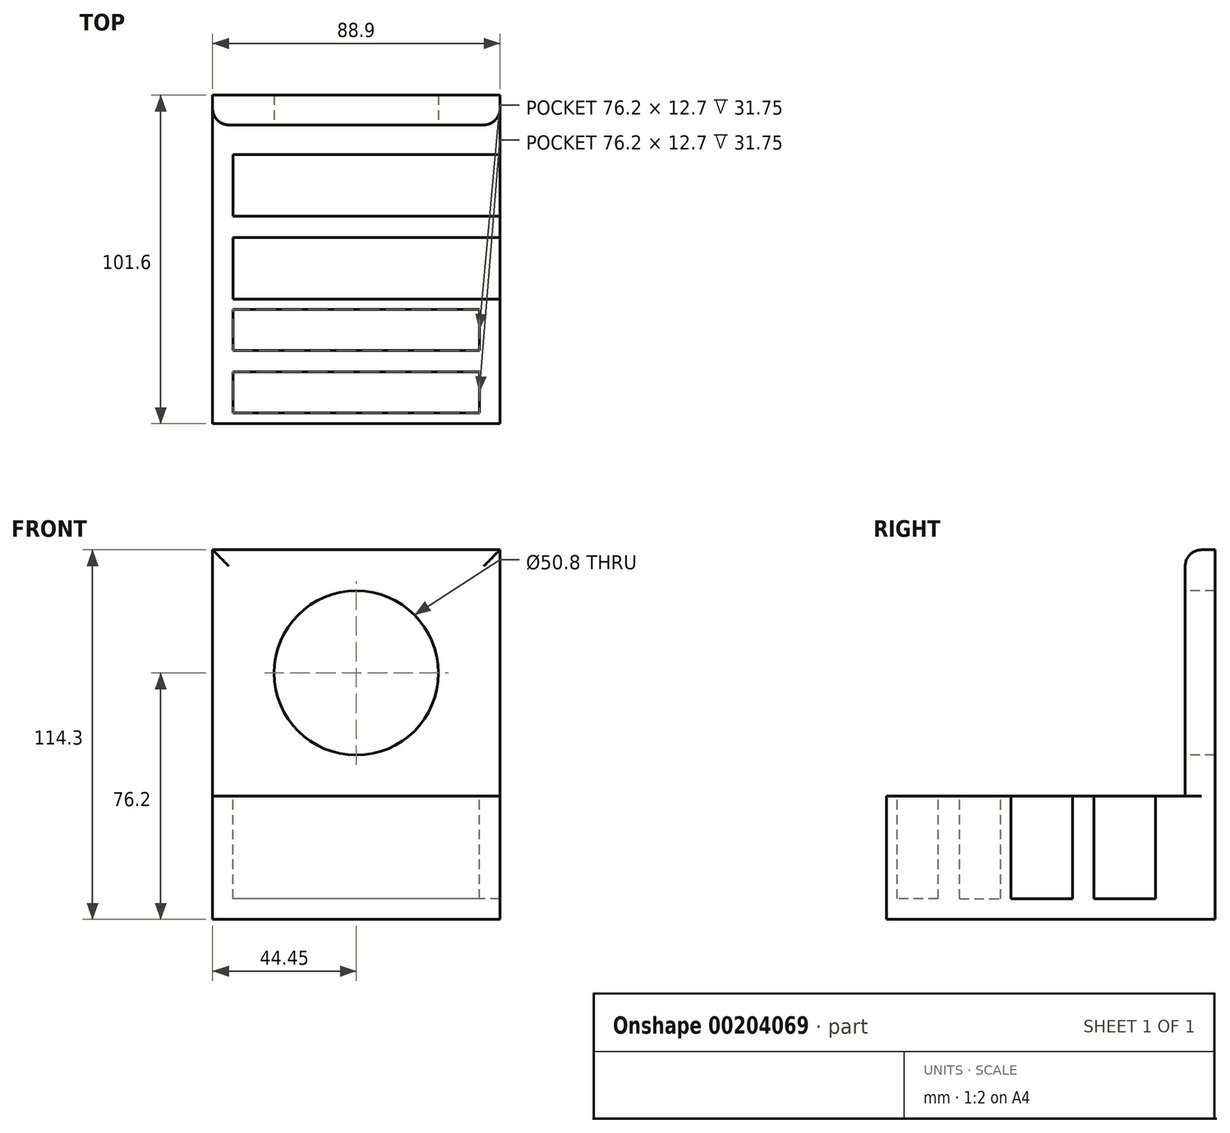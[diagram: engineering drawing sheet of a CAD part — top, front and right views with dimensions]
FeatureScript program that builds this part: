
annotation { "Feature Type Name" : "Feature", "Feature Type Description" : "" }
export const myFeature = defineFeature(function(context is Context, id is Id, definition is map)
    precondition{}
    {
        {
            var Q0;
            Q0=qCreatedBy(makeId("Front.planeOp"),FACE);
            var sketch = newSketch(context, id + "F0", { "sketchPlane" : qUnion([Q0])});
            skLineSegment(sketch, "E0", {"start": v(0, 19.05) * mm, "end": v(-44.45, 19.05) * mm});
            skLineSegment(sketch, "E1", {"start": v(-44.45, 19.05) * mm, "end": v(-44.45, 0) * mm});
            skLineSegment(sketch, "E2.MirrorCS", {"start": v(44.45, 19.05) * mm, "end": v(44.45, 0) * mm});
            skLineSegment(sketch, "E3.MirrorCS", {"start": v(0, 19.05) * mm, "end": v(44.45, 19.05) * mm});
            skLineSegment(sketch, "E4.MirrorCS", {"start": v(-44.45, -19.05) * mm, "end": v(-44.45, 0) * mm});
            skLineSegment(sketch, "E5.MirrorCS", {"start": v(0, -19.05) * mm, "end": v(-44.45, -19.05) * mm});
            skLineSegment(sketch, "E6.MirrorCS", {"start": v(0, -19.05) * mm, "end": v(44.45, -19.05) * mm});
            skLineSegment(sketch, "E7.MirrorCS", {"start": v(44.45, -19.05) * mm, "end": v(44.45, 0) * mm});
            skSolve(sketch);
        }
        {
            var Q0;
            Q0 = qSketchRegion(id + "F0", true);
            extrude(context, id + "F1", {"entities" : qUnion([Q0]), "depth" : 101.6 * mm});
        }
        {
            var Q0;
            Q0=makeQuery(id+"F1.opExtrude","SWEPT_FACE",FACE,{"disambiguationData":[OSD([sQuery(id+"F0.wireOp",EDGE,"E0"),sQuery(id+"F0.wireOp",EDGE,"E3.MirrorCS")])]});
            var sketch = newSketch(context, id + "F2", { "sketchPlane" : qUnion([Q0])});
            skLineSegment(sketch, "E8", {"start": v(0, 0) * mm, "end": v(0, -101.6) * mm, "construction": true});
            skLineSegment(sketch, "E9", {"start": v(0, -85.6) * mm, "end": v(-38.1, -85.6) * mm});
            skLineSegment(sketch, "E10", {"start": v(-38.1, -85.6) * mm, "end": v(-38.1, -98.3) * mm});
            skLineSegment(sketch, "E11", {"start": v(-38.1, -98.3) * mm, "end": v(0, -98.3) * mm});
            skLineSegment(sketch, "E12.MirrorCS", {"start": v(0, -85.6) * mm, "end": v(38.1, -85.6) * mm});
            skLineSegment(sketch, "E13.MirrorCS", {"start": v(38.1, -85.6) * mm, "end": v(38.1, -98.3) * mm});
            skLineSegment(sketch, "E14.MirrorCS", {"start": v(38.1, -98.3) * mm, "end": v(0, -98.3) * mm});
            skLineSegment(sketch, "E15", {"start": v(-44.45, -82.3) * mm, "end": v(44.45, -82.3) * mm, "construction": true});
            skLineSegment(sketch, "E16.MirrorCS", {"start": v(0, -79) * mm, "end": v(-38.1, -79) * mm});
            skLineSegment(sketch, "E17.MirrorCS", {"start": v(0, -79) * mm, "end": v(38.1, -79) * mm});
            skLineSegment(sketch, "E18.MirrorCS", {"start": v(38.1, -79) * mm, "end": v(38.1, -66.3) * mm});
            skLineSegment(sketch, "E19.MirrorCS", {"start": v(38.1, -66.3) * mm, "end": v(0, -66.3) * mm});
            skLineSegment(sketch, "E20.MirrorCS", {"start": v(-38.1, -66.3) * mm, "end": v(0, -66.3) * mm});
            skLineSegment(sketch, "E21.MirrorCS", {"start": v(-38.1, -79) * mm, "end": v(-38.1, -66.3) * mm});
            skSolve(sketch);
        }
        {
            var Q0;
            Q0 = qSketchRegion(id + "F2", true);
            extrude(context, id + "F3", {"entities" : qUnion([Q0]), "operationType" : NewBodyOperationType.REMOVE, "oppositeDirection" : true, "depth" : 31.75 * mm});
        }
        {
            var Q0;
            Q0=makeQuery(id+"F1.opExtrude","SWEPT_FACE",FACE,{"disambiguationData":[OSD([sQuery(id+"F0.wireOp",EDGE,"E1"),sQuery(id+"F0.wireOp",EDGE,"E4.MirrorCS")])]});
            var sketch = newSketch(context, id + "F4", { "sketchPlane" : qUnion([Q0])});
            skLineSegment(sketch, "E22.0.0", {"start": v(79, 19.05) * mm, "end": v(66.3, 19.05) * mm, "construction": true});
            skLineSegment(sketch, "E22.0.1", {"start": v(66.3, 19.05) * mm, "end": v(66.3, -12.7) * mm, "construction": true});
            skLineSegment(sketch, "E22.0.2", {"start": v(66.3, -12.7) * mm, "end": v(79, -12.7) * mm, "construction": true});
            skLineSegment(sketch, "E22.0.3", {"start": v(79, -12.7) * mm, "end": v(79, 19.05) * mm, "construction": true});
            skLineSegment(sketch, "E23.bottom", {"start": v(44.07, 19.05) * mm, "end": v(63.12, 19.05) * mm});
            skLineSegment(sketch, "E23.top", {"start": v(44.07, -12.7) * mm, "end": v(63.12, -12.7) * mm});
            skLineSegment(sketch, "E23.left", {"start": v(44.07, 19.05) * mm, "end": v(44.07, -12.7) * mm});
            skLineSegment(sketch, "E23.right", {"start": v(63.12, 19.05) * mm, "end": v(63.12, -12.7) * mm});
            skLineSegment(sketch, "E24", {"start": v(40.77, 19.05) * mm, "end": v(40.77, -19.05) * mm, "construction": true});
            skLineSegment(sketch, "E25.MirrorCS", {"start": v(37.47, 19.05) * mm, "end": v(18.42, 19.05) * mm});
            skLineSegment(sketch, "E26.MirrorCS", {"start": v(37.47, 19.05) * mm, "end": v(37.47, -12.7) * mm});
            skLineSegment(sketch, "E27.MirrorCS", {"start": v(37.47, -12.7) * mm, "end": v(18.42, -12.7) * mm});
            skLineSegment(sketch, "E28.MirrorCS", {"start": v(18.42, 19.05) * mm, "end": v(18.42, -12.7) * mm});
            skSolve(sketch);
        }
        {
            var Q0;
            Q0 = qSketchRegion(id + "F4", true);
            extrude(context, id + "F5", {"entities" : qUnion([Q0]), "operationType" : NewBodyOperationType.REMOVE, "endBound" : BoundingType.THROUGH_ALL, "oppositeDirection" : true, "depth" : 25.4 * mm});
        }
        {
            var Q0;
            {var subQ2=sQuery(id+"F0.wireOp",EDGE,"E3.MirrorCS");var subQ5=sQuery(id+"F0.wireOp",EDGE,"E0");Q0=makeQuery(id+"F5.boolean.opBoolean","SPLIT",FACE,{"disambiguationData":[TD([makeQuery(id+"F5.opExtrude","SWEPT_FACE",FACE,{"disambiguationData":[OSD([sQuery(id+"F4.wireOp",EDGE,"E28.MirrorCS")])]})])],"derivedFrom":makeQuery(id+"F1.opExtrude","SWEPT_FACE",FACE,{"disambiguationData":[OSD([subQ5,subQ2])]})});}
            var sketch = newSketch(context, id + "F6", { "sketchPlane" : qUnion([Q0])});
            skLineSegment(sketch, "E29.bottom", {"start": v(-44.45, 0) * mm, "end": v(44.45, 0) * mm});
            skLineSegment(sketch, "E29.top", {"start": v(-44.45, -9.2) * mm, "end": v(44.45, -9.2) * mm});
            skLineSegment(sketch, "E29.left", {"start": v(-44.45, 0) * mm, "end": v(-44.45, -9.2) * mm});
            skLineSegment(sketch, "E29.right", {"start": v(44.45, 0) * mm, "end": v(44.45, -9.2) * mm});
            skSolve(sketch);
        }
        {
            var Q0;
            Q0 = qSketchRegion(id + "F6", true);
            extrude(context, id + "F7", {"entities" : qUnion([Q0]), "operationType" : NewBodyOperationType.ADD, "depth" : 76.2 * mm});
        }
        {
            var Q0;
            Q0=makeQuery(id+"F7.boolean.opBoolean","MERGE",FACE,{"derivedFrom":[makeQuery(id+"F1.opExtrude","SWEPT_FACE",FACE,{"disambiguationData":[OSD([sQuery(id+"F0.wireOp",EDGE,"E1"),sQuery(id+"F0.wireOp",EDGE,"E4.MirrorCS")])]}),makeQuery(id+"F7.opExtrude","SWEPT_FACE",FACE,{"disambiguationData":[OSD([sQuery(id+"F6.wireOp",EDGE,"E29.left")])]})]});
            var sketch = newSketch(context, id + "F8", { "sketchPlane" : qUnion([Q0])});
            skLineSegment(sketch, "E30.bottom", {"start": v(18.42, 19.05) * mm, "end": v(37.47, 19.05) * mm});
            skLineSegment(sketch, "E30.top", {"start": v(18.42, -12.7) * mm, "end": v(37.47, -12.7) * mm});
            skLineSegment(sketch, "E30.left", {"start": v(18.42, 19.05) * mm, "end": v(18.42, -12.7) * mm});
            skLineSegment(sketch, "E30.right", {"start": v(37.47, 19.05) * mm, "end": v(37.47, -12.7) * mm});
            skLineSegment(sketch, "E31.bottom", {"start": v(44.07, 19.05) * mm, "end": v(63.12, 19.05) * mm});
            skLineSegment(sketch, "E31.top", {"start": v(44.07, -12.7) * mm, "end": v(63.12, -12.7) * mm});
            skLineSegment(sketch, "E31.left", {"start": v(44.07, 19.05) * mm, "end": v(44.07, -12.7) * mm});
            skLineSegment(sketch, "E31.right", {"start": v(63.12, 19.05) * mm, "end": v(63.12, -12.7) * mm});
            skSolve(sketch);
        }
        {
            var Q0;
            Q0 = qSketchRegion(id + "F8", true);
            var Q1;
            Q1=makeQuery(id+"F3.boolean.opBoolean","COPY",FACE,{"derivedFrom":makeQuery(id+"F3.opExtrude","SWEPT_FACE",FACE,{"disambiguationData":[OSD([sQuery(id+"F2.wireOp",EDGE,"E21.MirrorCS")])]})});
            extrude(context, id + "F9", {"entities" : qUnion([Q0]), "operationType" : NewBodyOperationType.ADD, "endBound" : BoundingType.UP_TO_SURFACE, "oppositeDirection" : true, "endBoundEntityFace" : qUnion([Q1]), "depth" : 25.4 * mm});
        }
        {
            var Q0;
            Q0=makeQuery(id+"F7.opExtrude","SWEPT_FACE",FACE,{"disambiguationData":[OSD([sQuery(id+"F6.wireOp",EDGE,"E29.top")])]});
            var sketch = newSketch(context, id + "F10", { "sketchPlane" : qUnion([Q0])});
            skCircle(sketch, "E32", {"center": v(0, 57.15) * mm, "radius": 25.4 * mm});
            skPoint(sketch, "E32.centerSnap0", {"position": v(-44.45, 57.15) * mm});
            skSolve(sketch);
        }
        {
            var Q0;
            Q0 = qSketchRegion(id + "F10", true);
            extrude(context, id + "F11", {"entities" : qUnion([Q0]), "operationType" : NewBodyOperationType.REMOVE, "endBound" : BoundingType.THROUGH_ALL, "oppositeDirection" : true, "depth" : 25.4 * mm});
        }
        {
            var Q0;
            Q0=makeQuery(id+"F7.opExtrude","CAP_EDGE",EDGE,{"disambiguationData":[OSD([sQuery(id+"F6.wireOp",EDGE,"E29.top")])],"isStart":false});
            var Q1;
            Q1=makeQuery(id+"F7.opExtrude","SWEPT_EDGE",EDGE,{"disambiguationData":[OSD([sQuery(id+"F0.wireOp",EDGE,"E0"),sQuery(id+"F0.wireOp",EDGE,"E1"),sQuery(id+"F6.wireOp",EDGE,"E29.top"),sQuery(id+"F6.wireOp",EDGE,"E29.left")])]});
            var Q2;
            Q2=makeQuery(id+"F7.opExtrude","SWEPT_EDGE",EDGE,{"disambiguationData":[OSD([sQuery(id+"F0.wireOp",EDGE,"E2.MirrorCS"),sQuery(id+"F0.wireOp",EDGE,"E3.MirrorCS"),sQuery(id+"F6.wireOp",EDGE,"E29.top"),sQuery(id+"F6.wireOp",EDGE,"E29.right")])]});
            var Q3;
            Q3=makeQuery(id+"F11.boolean.opBoolean","COPY",EDGE,{"derivedFrom":makeQuery(id+"F11.opExtrude","CAP_EDGE",EDGE,{"disambiguationData":[OSD([sQuery(id+"F10.wireOp",EDGE,"E32")])],"isStart":true})});
            fillet(context, id + "F12", {"entities" : qUnion([Q0, Q1, Q2, Q3]), "radius" : 5.08 * mm, "tangentPropagation" : true, "allowEdgeOverflow" : false});
        }
    });
